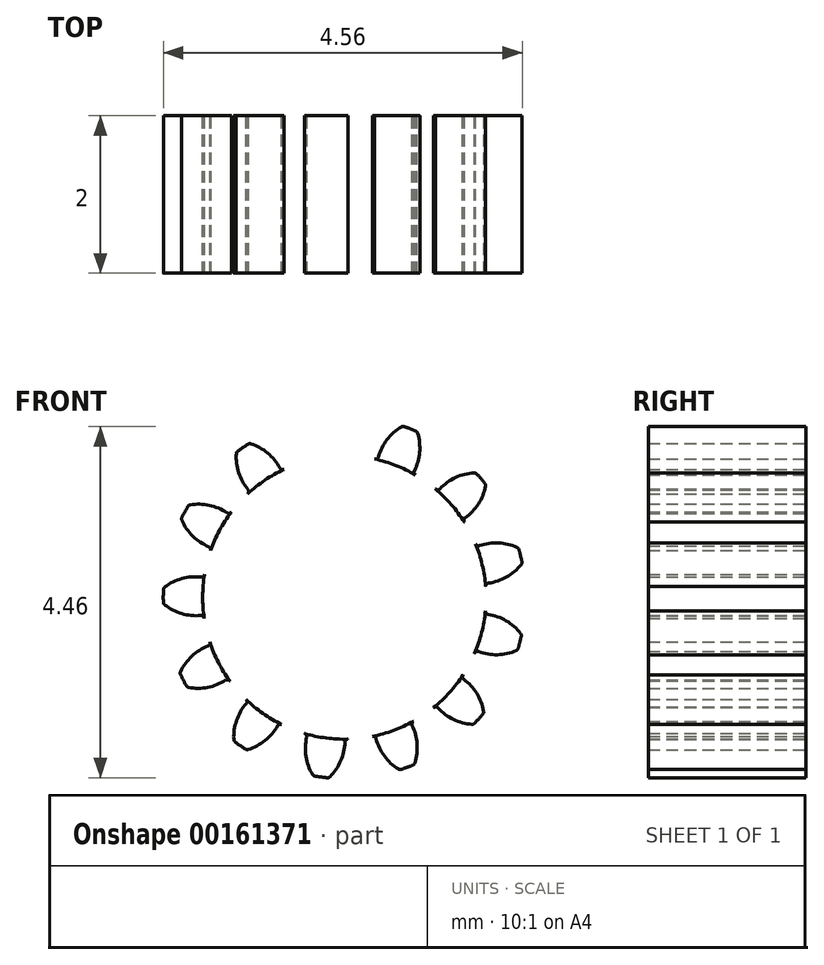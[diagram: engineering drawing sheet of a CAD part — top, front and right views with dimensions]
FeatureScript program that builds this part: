
annotation { "Feature Type Name" : "Feature", "Feature Type Description" : "" }
export const myFeature = defineFeature(function(context is Context, id is Id, definition is map)
    precondition{}
    {
        {
            var Q0;
            Q0=qCreatedBy(makeId("Front.planeOp"),FACE);
            var sketch = newSketch(context, id + "F0", { "sketchPlane" : qUnion([Q0])});
            skCircle(sketch, "E0", {"center": v(0, 0) * mm, "radius": 1.8 * mm, "construction": true});
            skCircle(sketch, "E1", {"center": v(0, 0) * mm, "radius": 2.05 * mm, "construction": true});
            skCircle(sketch, "E2", {"center": v(0, 0) * mm, "radius": 2.3 * mm, "construction": true});
            skLineSegment(sketch, "E3", {"start": v(0, 8.23) * mm, "end": v(0, 0) * mm, "construction": true});
            skCircle(sketch, "E4.cCircle", {"center": v(0, 0) * mm, "radius": 8.23 * mm, "construction": true});
            skLineSegment(sketch, "E4.0", {"start": v(0, 8.23) * mm, "end": v(1.83, 8.03) * mm, "construction": true});
            skLineSegment(sketch, "E4.1", {"start": v(1.83, 8.03) * mm, "end": v(3.57, 7.42) * mm, "construction": true});
            skLineSegment(sketch, "E4.2", {"start": v(3.57, 7.42) * mm, "end": v(5.13, 6.44) * mm, "construction": true});
            skLineSegment(sketch, "E4.3", {"start": v(5.13, 6.44) * mm, "end": v(6.44, 5.13) * mm, "construction": true});
            skLineSegment(sketch, "E4.4", {"start": v(6.44, 5.13) * mm, "end": v(7.42, 3.57) * mm, "construction": true});
            skLineSegment(sketch, "E4.5", {"start": v(7.42, 3.57) * mm, "end": v(8.03, 1.83) * mm, "construction": true});
            skLineSegment(sketch, "E4.6", {"start": v(8.03, 1.83) * mm, "end": v(8.23, 0) * mm, "construction": true});
            skLineSegment(sketch, "E4.7", {"start": v(8.23, 0) * mm, "end": v(8.03, -1.83) * mm, "construction": true});
            skLineSegment(sketch, "E4.8", {"start": v(8.03, -1.83) * mm, "end": v(7.42, -3.57) * mm, "construction": true});
            skLineSegment(sketch, "E4.9", {"start": v(7.42, -3.57) * mm, "end": v(6.44, -5.13) * mm, "construction": true});
            skLineSegment(sketch, "E4.10", {"start": v(6.44, -5.13) * mm, "end": v(5.13, -6.44) * mm, "construction": true});
            skLineSegment(sketch, "E4.11", {"start": v(5.13, -6.44) * mm, "end": v(3.57, -7.42) * mm, "construction": true});
            skLineSegment(sketch, "E4.12", {"start": v(3.57, -7.42) * mm, "end": v(1.83, -8.03) * mm, "construction": true});
            skLineSegment(sketch, "E4.13", {"start": v(1.83, -8.03) * mm, "end": v(0, -8.23) * mm, "construction": true});
            skLineSegment(sketch, "E4.14", {"start": v(0, -8.23) * mm, "end": v(-1.83, -8.03) * mm, "construction": true});
            skLineSegment(sketch, "E4.15", {"start": v(-1.83, -8.03) * mm, "end": v(-3.57, -7.42) * mm, "construction": true});
            skLineSegment(sketch, "E4.16", {"start": v(-3.57, -7.42) * mm, "end": v(-5.13, -6.44) * mm, "construction": true});
            skLineSegment(sketch, "E4.17", {"start": v(-5.13, -6.44) * mm, "end": v(-6.44, -5.13) * mm, "construction": true});
            skLineSegment(sketch, "E4.18", {"start": v(-6.44, -5.13) * mm, "end": v(-7.42, -3.57) * mm, "construction": true});
            skLineSegment(sketch, "E4.19", {"start": v(-7.42, -3.57) * mm, "end": v(-8.03, -1.83) * mm, "construction": true});
            skLineSegment(sketch, "E4.20", {"start": v(-8.03, -1.83) * mm, "end": v(-8.23, 0) * mm, "construction": true});
            skLineSegment(sketch, "E4.21", {"start": v(-8.23, 0) * mm, "end": v(-8.03, 1.83) * mm, "construction": true});
            skLineSegment(sketch, "E4.22", {"start": v(-8.03, 1.83) * mm, "end": v(-7.42, 3.57) * mm, "construction": true});
            skLineSegment(sketch, "E4.23", {"start": v(-7.42, 3.57) * mm, "end": v(-6.44, 5.13) * mm, "construction": true});
            skLineSegment(sketch, "E4.24", {"start": v(-6.44, 5.13) * mm, "end": v(-5.13, 6.44) * mm, "construction": true});
            skLineSegment(sketch, "E4.25", {"start": v(-5.13, 6.44) * mm, "end": v(-3.57, 7.42) * mm, "construction": true});
            skLineSegment(sketch, "E4.26", {"start": v(-3.57, 7.42) * mm, "end": v(-1.83, 8.03) * mm, "construction": true});
            skLineSegment(sketch, "E4.27", {"start": v(-1.83, 8.03) * mm, "end": v(0, 8.23) * mm, "construction": true});
            skLineSegment(sketch, "E5.0", {"start": v(-0.93, 8.23) * mm, "end": v(0.93, 8.23) * mm, "construction": true});
            skLineSegment(sketch, "E5.1", {"start": v(0.93, 8.23) * mm, "end": v(2.74, 7.82) * mm, "construction": true});
            skLineSegment(sketch, "E5.2", {"start": v(2.74, 7.82) * mm, "end": v(4.4, 7.02) * mm, "construction": true});
            skLineSegment(sketch, "E5.3", {"start": v(4.4, 7.02) * mm, "end": v(5.86, 5.86) * mm});
            skLineSegment(sketch, "E5.4", {"start": v(5.86, 5.86) * mm, "end": v(7.02, 4.4) * mm});
            skLineSegment(sketch, "E5.5", {"start": v(7.02, 4.4) * mm, "end": v(7.82, 2.74) * mm});
            skLineSegment(sketch, "E5.6", {"start": v(7.82, 2.74) * mm, "end": v(8.23, 0.93) * mm});
            skLineSegment(sketch, "E5.7", {"start": v(8.23, 0.93) * mm, "end": v(8.23, -0.93) * mm});
            skLineSegment(sketch, "E5.8", {"start": v(8.23, -0.93) * mm, "end": v(7.82, -2.74) * mm});
            skLineSegment(sketch, "E5.9", {"start": v(7.82, -2.74) * mm, "end": v(7.02, -4.4) * mm});
            skLineSegment(sketch, "E5.10", {"start": v(7.02, -4.4) * mm, "end": v(5.86, -5.86) * mm});
            skLineSegment(sketch, "E5.11", {"start": v(5.86, -5.86) * mm, "end": v(4.4, -7.02) * mm});
            skLineSegment(sketch, "E5.12", {"start": v(4.4, -7.02) * mm, "end": v(2.74, -7.82) * mm});
            skLineSegment(sketch, "E5.13", {"start": v(2.74, -7.82) * mm, "end": v(0.93, -8.23) * mm});
            skLineSegment(sketch, "E5.14", {"start": v(0.93, -8.23) * mm, "end": v(-0.93, -8.23) * mm});
            skLineSegment(sketch, "E5.15", {"start": v(-0.93, -8.23) * mm, "end": v(-2.74, -7.82) * mm});
            skLineSegment(sketch, "E5.16", {"start": v(-2.74, -7.82) * mm, "end": v(-4.4, -7.02) * mm});
            skLineSegment(sketch, "E5.17", {"start": v(-4.4, -7.02) * mm, "end": v(-5.86, -5.86) * mm});
            skLineSegment(sketch, "E5.18", {"start": v(-5.86, -5.86) * mm, "end": v(-7.02, -4.4) * mm});
            skLineSegment(sketch, "E5.19", {"start": v(-7.02, -4.4) * mm, "end": v(-7.82, -2.74) * mm});
            skLineSegment(sketch, "E5.20", {"start": v(-7.82, -2.74) * mm, "end": v(-8.23, -0.93) * mm});
            skLineSegment(sketch, "E5.21", {"start": v(-8.23, -0.93) * mm, "end": v(-8.23, 0.93) * mm});
            skLineSegment(sketch, "E5.22", {"start": v(-8.23, 0.93) * mm, "end": v(-7.82, 2.74) * mm});
            skLineSegment(sketch, "E5.23", {"start": v(-7.82, 2.74) * mm, "end": v(-7.02, 4.4) * mm});
            skLineSegment(sketch, "E5.24", {"start": v(-7.02, 4.4) * mm, "end": v(-5.86, 5.86) * mm});
            skLineSegment(sketch, "E5.25", {"start": v(-5.86, 5.86) * mm, "end": v(-4.4, 7.02) * mm, "construction": true});
            skLineSegment(sketch, "E5.26", {"start": v(-4.4, 7.02) * mm, "end": v(-2.74, 7.82) * mm, "construction": true});
            skLineSegment(sketch, "E5.27", {"start": v(-2.74, 7.82) * mm, "end": v(-0.93, 8.23) * mm, "construction": true});
            skPoint(sketch, "E5.0.midPoint", {"position": v(0, 8.23) * mm});
            skLineSegment(sketch, "E6", {"start": v(-0.93, 8.23) * mm, "end": v(0, 0) * mm, "construction": true});
            skLineSegment(sketch, "E7", {"start": v(0, 2.05) * mm, "end": v(-9.32, 2.05) * mm, "construction": true});
            skLineSegment(sketch, "E8", {"start": v(0, 2.05) * mm, "end": v(-5.63, 0) * mm, "construction": true});
            skCircle(sketch, "E9", {"center": v(0, 2.05) * mm, "radius": 0.65 * mm, "construction": true});
            skCircle(sketch, "E10", {"center": v(-0.61, 1.83) * mm, "radius": 0.65 * mm, "construction": true});
            skArc(sketch, "E11", {"start": v(-0.15, 2.28) * mm, "mid": v(-0.01, 2.08) * mm, "end": v(0.04, 1.84) * mm});
            skArc(sketch, "E12.MirrorCS", {"start": v(-0.36, 2.27) * mm, "mid": v(-0.45, 2.02) * mm, "end": v(-0.44, 1.75) * mm});
            skArc(sketch, "E13.MirrorCS", {"start": v(-0.37, 2.26) * mm, "mid": v(-0.45, 2.03) * mm, "end": v(-0.45, 1.78) * mm});
            skArc(sketch, "E14", {"start": v(-0.34, 2.28) * mm, "mid": v(-0.26, 2.29) * mm, "end": v(-0.18, 2.3) * mm});
            skArc(sketch, "E15", {"start": v(-0.48, 1.74) * mm, "mid": v(0.2, -1.79) * mm, "end": v(0.08, 1.8) * mm});
            skPoint(sketch, "E16.visualSharp", {"position": v(-0.44, 1.75) * mm});
            skArc(sketch, "E16.filletArc", {"start": v(-0.48, 1.74) * mm, "mid": v(-0.45, 1.75) * mm, "end": v(-0.45, 1.78) * mm});
            skPoint(sketch, "E17.visualSharp", {"position": v(0.04, 1.8) * mm});
            skArc(sketch, "E17.filletArc", {"start": v(0.04, 1.84) * mm, "mid": v(0.05, 1.81) * mm, "end": v(0.08, 1.8) * mm});
            skPoint(sketch, "E18.visualSharp", {"position": v(-0.36, 2.27) * mm});
            skArc(sketch, "E18.filletArc", {"start": v(-0.34, 2.28) * mm, "mid": v(-0.35, 2.27) * mm, "end": v(-0.37, 2.26) * mm});
            skPoint(sketch, "E19.visualSharp", {"position": v(-0.16, 2.3) * mm});
            skArc(sketch, "E19.filletArc", {"start": v(-0.15, 2.28) * mm, "mid": v(-0.16, 2.3) * mm, "end": v(-0.18, 2.3) * mm});
            skArc(sketch, "E20.1.0", {"start": v(-1.37, 1.83) * mm, "mid": v(-1.34, 1.59) * mm, "end": v(-1.22, 1.37) * mm});
            skArc(sketch, "E20.1.1", {"start": v(-1.23, 1.32) * mm, "mid": v(-1.22, 1.34) * mm, "end": v(-1.22, 1.37) * mm});
            skArc(sketch, "E20.1.2", {"start": v(-1.36, 1.86) * mm, "mid": v(-1.37, 1.84) * mm, "end": v(-1.37, 1.83) * mm});
            skArc(sketch, "E20.1.3", {"start": v(-1.36, 1.86) * mm, "mid": v(-1.3, 1.9) * mm, "end": v(-1.22, 1.95) * mm});
            skArc(sketch, "E20.1.4", {"start": v(-1.19, 1.95) * mm, "mid": v(-0.97, 1.83) * mm, "end": v(-0.82, 1.65) * mm});
            skArc(sketch, "E20.1.5", {"start": v(-1.19, 1.95) * mm, "mid": v(-1.2, 1.95) * mm, "end": v(-1.22, 1.95) * mm});
            skArc(sketch, "E20.1.6", {"start": v(-0.82, 1.65) * mm, "mid": v(-0.8, 1.63) * mm, "end": v(-0.77, 1.63) * mm});
            skArc(sketch, "E20.2.0", {"start": v(-2.06, 0.98) * mm, "mid": v(-1.93, 0.78) * mm, "end": v(-1.72, 0.64) * mm});
            skArc(sketch, "E20.2.1", {"start": v(-1.7, 0.6) * mm, "mid": v(-1.7, 0.62) * mm, "end": v(-1.72, 0.64) * mm});
            skArc(sketch, "E20.2.2", {"start": v(-2.06, 1.01) * mm, "mid": v(-2.07, 1) * mm, "end": v(-2.06, 0.98) * mm});
            skArc(sketch, "E20.2.3", {"start": v(-2.06, 1.01) * mm, "mid": v(-2.03, 1.09) * mm, "end": v(-1.99, 1.16) * mm});
            skArc(sketch, "E20.2.4", {"start": v(-1.96, 1.18) * mm, "mid": v(-1.72, 1.17) * mm, "end": v(-1.5, 1.08) * mm});
            skArc(sketch, "E20.2.5", {"start": v(-1.96, 1.18) * mm, "mid": v(-1.98, 1.17) * mm, "end": v(-1.99, 1.16) * mm});
            skArc(sketch, "E20.2.6", {"start": v(-1.5, 1.08) * mm, "mid": v(-1.46, 1.07) * mm, "end": v(-1.44, 1.09) * mm});
            skArc(sketch, "E20.3.0", {"start": v(-2.28, -0.1) * mm, "mid": v(-2.07, -0.2) * mm, "end": v(-1.82, -0.23) * mm});
            skArc(sketch, "E20.3.1", {"start": v(-1.78, -0.26) * mm, "mid": v(-1.8, -0.24) * mm, "end": v(-1.82, -0.23) * mm});
            skArc(sketch, "E20.3.2", {"start": v(-2.3, -0.06) * mm, "mid": v(-2.3, -0.08) * mm, "end": v(-2.28, -0.1) * mm});
            skArc(sketch, "E20.3.3", {"start": v(-2.3, -0.06) * mm, "mid": v(-2.3, 0.02) * mm, "end": v(-2.3, 0.1) * mm});
            skArc(sketch, "E20.3.4", {"start": v(-2.28, 0.13) * mm, "mid": v(-2.06, 0.24) * mm, "end": v(-1.82, 0.26) * mm});
            skArc(sketch, "E20.3.5", {"start": v(-2.28, 0.13) * mm, "mid": v(-2.3, 0.12) * mm, "end": v(-2.3, 0.1) * mm});
            skArc(sketch, "E20.3.6", {"start": v(-1.82, 0.26) * mm, "mid": v(-1.8, 0.27) * mm, "end": v(-1.78, 0.3) * mm});
            skArc(sketch, "E20.4.0", {"start": v(-1.98, -1.14) * mm, "mid": v(-1.74, -1.14) * mm, "end": v(-1.5, -1.05) * mm});
            skArc(sketch, "E20.4.1", {"start": v(-1.45, -1.06) * mm, "mid": v(-1.48, -1.04) * mm, "end": v(-1.5, -1.05) * mm});
            skArc(sketch, "E20.4.2", {"start": v(-2, -1.12) * mm, "mid": v(-2, -1.14) * mm, "end": v(-1.98, -1.14) * mm});
            skArc(sketch, "E20.4.3", {"start": v(-2, -1.12) * mm, "mid": v(-2.05, -1.05) * mm, "end": v(-2.08, -0.98) * mm});
            skArc(sketch, "E20.4.4", {"start": v(-2.08, -0.94) * mm, "mid": v(-1.94, -0.75) * mm, "end": v(-1.73, -0.62) * mm});
            skArc(sketch, "E20.4.5", {"start": v(-2.08, -0.94) * mm, "mid": v(-2.09, -0.96) * mm, "end": v(-2.08, -0.98) * mm});
            skArc(sketch, "E20.4.6", {"start": v(-1.73, -0.62) * mm, "mid": v(-1.71, -0.6) * mm, "end": v(-1.7, -0.57) * mm});
            skArc(sketch, "E20.5.0", {"start": v(-1.22, -1.93) * mm, "mid": v(-1, -1.82) * mm, "end": v(-0.85, -1.63) * mm});
            skArc(sketch, "E20.5.1", {"start": v(-0.8, -1.61) * mm, "mid": v(-0.82, -1.61) * mm, "end": v(-0.85, -1.63) * mm});
            skArc(sketch, "E20.5.2", {"start": v(-1.26, -1.93) * mm, "mid": v(-1.24, -1.93) * mm, "end": v(-1.22, -1.93) * mm});
            skArc(sketch, "E20.5.3", {"start": v(-1.26, -1.93) * mm, "mid": v(-1.32, -1.88) * mm, "end": v(-1.39, -1.83) * mm});
            skArc(sketch, "E20.5.4", {"start": v(-1.4, -1.8) * mm, "mid": v(-1.37, -1.56) * mm, "end": v(-1.25, -1.35) * mm});
            skArc(sketch, "E20.5.5", {"start": v(-1.4, -1.8) * mm, "mid": v(-1.4, -1.82) * mm, "end": v(-1.39, -1.83) * mm});
            skArc(sketch, "E20.5.6", {"start": v(-1.25, -1.35) * mm, "mid": v(-1.24, -1.32) * mm, "end": v(-1.25, -1.3) * mm});
            skArc(sketch, "E20.6.0", {"start": v(-0.18, -2.28) * mm, "mid": v(-0.05, -2.08) * mm, "end": v(0, -1.84) * mm});
            skArc(sketch, "E20.6.1", {"start": v(0.05, -1.8) * mm, "mid": v(0.02, -1.81) * mm, "end": v(0, -1.84) * mm});
            skArc(sketch, "E20.6.2", {"start": v(-0.22, -2.29) * mm, "mid": v(-0.2, -2.29) * mm, "end": v(-0.18, -2.28) * mm});
            skArc(sketch, "E20.6.3", {"start": v(-0.22, -2.29) * mm, "mid": v(-0.3, -2.28) * mm, "end": v(-0.38, -2.27) * mm});
            skArc(sketch, "E20.6.4", {"start": v(-0.4, -2.25) * mm, "mid": v(-0.49, -2.02) * mm, "end": v(-0.48, -1.77) * mm});
            skArc(sketch, "E20.6.5", {"start": v(-0.4, -2.25) * mm, "mid": v(-0.4, -2.26) * mm, "end": v(-0.38, -2.27) * mm});
            skArc(sketch, "E20.6.6", {"start": v(-0.48, -1.77) * mm, "mid": v(-0.48, -1.75) * mm, "end": v(-0.5, -1.73) * mm});
            skArc(sketch, "E20.7.0", {"start": v(0.9, -2.1) * mm, "mid": v(0.92, -1.86) * mm, "end": v(0.86, -1.62) * mm});
            skArc(sketch, "E20.7.1", {"start": v(0.88, -1.57) * mm, "mid": v(0.86, -1.6) * mm, "end": v(0.86, -1.62) * mm});
            skArc(sketch, "E20.7.2", {"start": v(0.87, -2.13) * mm, "mid": v(0.89, -2.12) * mm, "end": v(0.9, -2.1) * mm});
            skArc(sketch, "E20.7.3", {"start": v(0.87, -2.13) * mm, "mid": v(0.8, -2.16) * mm, "end": v(0.72, -2.18) * mm});
            skArc(sketch, "E20.7.4", {"start": v(0.69, -2.18) * mm, "mid": v(0.5, -2.01) * mm, "end": v(0.4, -1.8) * mm});
            skArc(sketch, "E20.7.5", {"start": v(0.69, -2.18) * mm, "mid": v(0.7, -2.19) * mm, "end": v(0.72, -2.18) * mm});
            skArc(sketch, "E20.7.6", {"start": v(0.4, -1.8) * mm, "mid": v(0.38, -1.77) * mm, "end": v(0.36, -1.76) * mm});
            skArc(sketch, "E20.8.0", {"start": v(1.77, -1.45) * mm, "mid": v(1.68, -1.22) * mm, "end": v(1.52, -1.04) * mm});
            skArc(sketch, "E20.8.1", {"start": v(1.5, -0.98) * mm, "mid": v(1.5, -1.01) * mm, "end": v(1.52, -1.04) * mm});
            skArc(sketch, "E20.8.2", {"start": v(1.76, -1.48) * mm, "mid": v(1.77, -1.46) * mm, "end": v(1.77, -1.45) * mm});
            skArc(sketch, "E20.8.3", {"start": v(1.76, -1.48) * mm, "mid": v(1.7, -1.54) * mm, "end": v(1.65, -1.6) * mm});
            skArc(sketch, "E20.8.4", {"start": v(1.62, -1.61) * mm, "mid": v(1.39, -1.55) * mm, "end": v(1.19, -1.4) * mm});
            skArc(sketch, "E20.8.5", {"start": v(1.62, -1.61) * mm, "mid": v(1.64, -1.6) * mm, "end": v(1.65, -1.6) * mm});
            skArc(sketch, "E20.8.6", {"start": v(1.19, -1.4) * mm, "mid": v(1.16, -1.39) * mm, "end": v(1.13, -1.4) * mm});
            skArc(sketch, "E20.9.0", {"start": v(2.24, -0.46) * mm, "mid": v(2.06, -0.3) * mm, "end": v(1.83, -0.21) * mm});
            skArc(sketch, "E20.9.1", {"start": v(1.8, -0.17) * mm, "mid": v(1.8, -0.2) * mm, "end": v(1.83, -0.21) * mm});
            skArc(sketch, "E20.9.2", {"start": v(2.25, -0.5) * mm, "mid": v(2.25, -0.47) * mm, "end": v(2.24, -0.46) * mm});
            skArc(sketch, "E20.9.3", {"start": v(2.25, -0.5) * mm, "mid": v(2.23, -0.57) * mm, "end": v(2.2, -0.65) * mm});
            skArc(sketch, "E20.9.4", {"start": v(2.18, -0.67) * mm, "mid": v(1.95, -0.73) * mm, "end": v(1.7, -0.69) * mm});
            skArc(sketch, "E20.9.5", {"start": v(2.18, -0.67) * mm, "mid": v(2.2, -0.66) * mm, "end": v(2.2, -0.65) * mm});
            skArc(sketch, "E20.9.6", {"start": v(1.7, -0.69) * mm, "mid": v(1.67, -0.69) * mm, "end": v(1.65, -0.71) * mm});
            skArc(sketch, "E20.10.0", {"start": v(2.2, 0.64) * mm, "mid": v(1.96, 0.7) * mm, "end": v(1.72, 0.66) * mm});
            skArc(sketch, "E20.10.1", {"start": v(1.67, 0.68) * mm, "mid": v(1.69, 0.66) * mm, "end": v(1.72, 0.66) * mm});
            skArc(sketch, "E20.10.2", {"start": v(2.22, 0.6) * mm, "mid": v(2.2, 0.62) * mm, "end": v(2.2, 0.64) * mm});
            skArc(sketch, "E20.10.3", {"start": v(2.22, 0.6) * mm, "mid": v(2.24, 0.53) * mm, "end": v(2.26, 0.45) * mm});
            skArc(sketch, "E20.10.4", {"start": v(2.25, 0.42) * mm, "mid": v(2.06, 0.26) * mm, "end": v(1.83, 0.18) * mm});
            skArc(sketch, "E20.10.5", {"start": v(2.25, 0.42) * mm, "mid": v(2.25, 0.43) * mm, "end": v(2.26, 0.45) * mm});
            skArc(sketch, "E20.10.6", {"start": v(1.83, 0.18) * mm, "mid": v(1.8, 0.17) * mm, "end": v(1.8, 0.14) * mm});
            skArc(sketch, "E20.11.0", {"start": v(1.65, 1.58) * mm, "mid": v(1.41, 1.52) * mm, "end": v(1.21, 1.38) * mm});
            skArc(sketch, "E20.11.1", {"start": v(1.16, 1.38) * mm, "mid": v(1.19, 1.37) * mm, "end": v(1.21, 1.38) * mm});
            skArc(sketch, "E20.11.2", {"start": v(1.68, 1.57) * mm, "mid": v(1.67, 1.58) * mm, "end": v(1.65, 1.58) * mm});
            skArc(sketch, "E20.11.3", {"start": v(1.68, 1.57) * mm, "mid": v(1.73, 1.51) * mm, "end": v(1.79, 1.45) * mm});
            skArc(sketch, "E20.11.4", {"start": v(1.8, 1.42) * mm, "mid": v(1.7, 1.19) * mm, "end": v(1.53, 1.01) * mm});
            skArc(sketch, "E20.11.5", {"start": v(1.8, 1.42) * mm, "mid": v(1.8, 1.43) * mm, "end": v(1.79, 1.45) * mm});
            skArc(sketch, "E20.11.6", {"start": v(1.53, 1.01) * mm, "mid": v(1.52, 0.99) * mm, "end": v(1.52, 0.96) * mm});
            skArc(sketch, "E20.12.0", {"start": v(0.72, 2.17) * mm, "mid": v(0.54, 2) * mm, "end": v(0.43, 1.79) * mm});
            skArc(sketch, "E20.12.1", {"start": v(0.39, 1.76) * mm, "mid": v(0.41, 1.76) * mm, "end": v(0.43, 1.79) * mm});
            skArc(sketch, "E20.12.2", {"start": v(0.76, 2.17) * mm, "mid": v(0.74, 2.17) * mm, "end": v(0.72, 2.17) * mm});
            skArc(sketch, "E20.12.3", {"start": v(0.76, 2.17) * mm, "mid": v(0.83, 2.14) * mm, "end": v(0.9, 2.11) * mm});
            skArc(sketch, "E20.12.4", {"start": v(0.93, 2.09) * mm, "mid": v(0.96, 1.84) * mm, "end": v(0.89, 1.6) * mm});
            skArc(sketch, "E20.12.5", {"start": v(0.93, 2.09) * mm, "mid": v(0.92, 2.1) * mm, "end": v(0.9, 2.11) * mm});
            skArc(sketch, "E20.12.6", {"start": v(0.89, 1.6) * mm, "mid": v(0.89, 1.58) * mm, "end": v(0.9, 1.56) * mm});
            skSolve(sketch);
        }
        {
            var Q0;
            Q0=makeQuery(id+"F0.imprint","IMPRINT",FACE,{"disambiguationData":[TD([[makeQuery(id+"F0.imprint","IMPRINT",EDGE,{"derivedFrom":sQuery(id+"F0.wireOp",EDGE,"E11")}),-1.0]])]});
            var Q1;
            Q1=makeQuery(id+"F0.imprint","IMPRINT",FACE,{"disambiguationData":[TD([[makeQuery(id+"F0.imprint","IMPRINT",EDGE,{"derivedFrom":sQuery(id+"F0.wireOp",EDGE,"E20.1.0")}),1.0]])]});
            var Q2;
            Q2=makeQuery(id+"F0.imprint","IMPRINT",FACE,{"disambiguationData":[TD([[makeQuery(id+"F0.imprint","IMPRINT",EDGE,{"derivedFrom":sQuery(id+"F0.wireOp",EDGE,"E20.3.0")}),1.0]])]});
            var Q3;
            Q3=makeQuery(id+"F0.imprint","IMPRINT",FACE,{"disambiguationData":[TD([[makeQuery(id+"F0.imprint","IMPRINT",EDGE,{"derivedFrom":sQuery(id+"F0.wireOp",EDGE,"E20.5.0")}),1.0]])]});
            var Q4;
            Q4=makeQuery(id+"F0.imprint","IMPRINT",FACE,{"disambiguationData":[TD([[makeQuery(id+"F0.imprint","IMPRINT",EDGE,{"derivedFrom":sQuery(id+"F0.wireOp",EDGE,"E20.6.0")}),1.0]])]});
            var Q5;
            Q5=makeQuery(id+"F0.imprint","IMPRINT",FACE,{"disambiguationData":[TD([[makeQuery(id+"F0.imprint","IMPRINT",EDGE,{"derivedFrom":sQuery(id+"F0.wireOp",EDGE,"E20.7.0")}),1.0]])]});
            var Q6;
            Q6=makeQuery(id+"F0.imprint","IMPRINT",FACE,{"disambiguationData":[TD([[makeQuery(id+"F0.imprint","IMPRINT",EDGE,{"derivedFrom":sQuery(id+"F0.wireOp",EDGE,"E20.8.0")}),1.0]])]});
            var Q7;
            Q7=makeQuery(id+"F0.imprint","IMPRINT",FACE,{"disambiguationData":[TD([[makeQuery(id+"F0.imprint","IMPRINT",EDGE,{"derivedFrom":sQuery(id+"F0.wireOp",EDGE,"E20.9.0")}),1.0]])]});
            var Q8;
            Q8=makeQuery(id+"F0.imprint","IMPRINT",FACE,{"disambiguationData":[TD([[makeQuery(id+"F0.imprint","IMPRINT",EDGE,{"derivedFrom":sQuery(id+"F0.wireOp",EDGE,"E20.10.0")}),1.0]])]});
            var Q9;
            Q9=makeQuery(id+"F0.imprint","IMPRINT",FACE,{"disambiguationData":[TD([[makeQuery(id+"F0.imprint","IMPRINT",EDGE,{"derivedFrom":sQuery(id+"F0.wireOp",EDGE,"E20.11.0")}),1.0]])]});
            var Q10;
            Q10=makeQuery(id+"F0.imprint","IMPRINT",FACE,{"disambiguationData":[TD([[makeQuery(id+"F0.imprint","IMPRINT",EDGE,{"derivedFrom":sQuery(id+"F0.wireOp",EDGE,"E20.12.0")}),1.0]])]});
            var Q11;
            Q11=makeQuery(id+"F0.imprint","IMPRINT",FACE,{"disambiguationData":[TD([[makeQuery(id+"F0.imprint","IMPRINT",EDGE,{"derivedFrom":sQuery(id+"F0.wireOp",EDGE,"E20.13.0")}),1.0]])]});
            var Q12;
            Q12=makeQuery(id+"F0.imprint","IMPRINT",FACE,{"disambiguationData":[TD([[makeQuery(id+"F0.imprint","IMPRINT",EDGE,{"derivedFrom":sQuery(id+"F0.wireOp",EDGE,"E20.2.0")}),1.0]])]});
            var Q13;
            Q13=makeQuery(id+"F0.imprint","IMPRINT",FACE,{"disambiguationData":[TD([[makeQuery(id+"F0.imprint","IMPRINT",EDGE,{"derivedFrom":sQuery(id+"F0.wireOp",EDGE,"E20.4.0")}),1.0]])]});
            extrude(context, id + "F1", {"entities" : qUnion([Q0, Q1, Q2, Q3, Q4, Q5, Q6, Q7, Q8, Q9, Q10, Q11, Q12, Q13]), "depth" : 2 * mm});
        }
        {
            var Q0;
            Q0=makeQuery(id+"F1.opExtrude","CAP_FACE",FACE,{"disambiguationData":[OSD([sQuery(id+"F0.wireOp",EDGE,"E11"),sQuery(id+"F0.wireOp",EDGE,"E13.MirrorCS"),sQuery(id+"F0.wireOp",EDGE,"E14"),sQuery(id+"F0.wireOp",EDGE,"E15"),sQuery(id+"F0.wireOp",EDGE,"E16.filletArc"),sQuery(id+"F0.wireOp",EDGE,"E17.filletArc"),sQuery(id+"F0.wireOp",EDGE,"E18.filletArc"),sQuery(id+"F0.wireOp",EDGE,"E19.filletArc"),sQuery(id+"F0.wireOp",EDGE,"E20.1.0"),sQuery(id+"F0.wireOp",EDGE,"E20.1.1"),sQuery(id+"F0.wireOp",EDGE,"E20.1.2"),sQuery(id+"F0.wireOp",EDGE,"E20.1.3"),sQuery(id+"F0.wireOp",EDGE,"E20.1.4"),sQuery(id+"F0.wireOp",EDGE,"E20.1.5"),sQuery(id+"F0.wireOp",EDGE,"E20.1.6"),sQuery(id+"F0.wireOp",EDGE,"E20.2.0"),sQuery(id+"F0.wireOp",EDGE,"E20.2.1"),sQuery(id+"F0.wireOp",EDGE,"E20.2.2"),sQuery(id+"F0.wireOp",EDGE,"E20.2.3"),sQuery(id+"F0.wireOp",EDGE,"E20.2.4"),sQuery(id+"F0.wireOp",EDGE,"E20.2.5"),sQuery(id+"F0.wireOp",EDGE,"E20.2.6"),sQuery(id+"F0.wireOp",EDGE,"E20.3.0"),sQuery(id+"F0.wireOp",EDGE,"E20.3.1"),sQuery(id+"F0.wireOp",EDGE,"E20.3.2"),sQuery(id+"F0.wireOp",EDGE,"E20.3.3"),sQuery(id+"F0.wireOp",EDGE,"E20.3.4"),sQuery(id+"F0.wireOp",EDGE,"E20.3.5"),sQuery(id+"F0.wireOp",EDGE,"E20.3.6"),sQuery(id+"F0.wireOp",EDGE,"E20.4.0"),sQuery(id+"F0.wireOp",EDGE,"E20.4.1"),sQuery(id+"F0.wireOp",EDGE,"E20.4.2"),sQuery(id+"F0.wireOp",EDGE,"E20.4.3"),sQuery(id+"F0.wireOp",EDGE,"E20.4.4"),sQuery(id+"F0.wireOp",EDGE,"E20.4.5"),sQuery(id+"F0.wireOp",EDGE,"E20.4.6"),sQuery(id+"F0.wireOp",EDGE,"E20.5.0"),sQuery(id+"F0.wireOp",EDGE,"E20.5.1"),sQuery(id+"F0.wireOp",EDGE,"E20.5.2"),sQuery(id+"F0.wireOp",EDGE,"E20.5.3"),sQuery(id+"F0.wireOp",EDGE,"E20.5.4"),sQuery(id+"F0.wireOp",EDGE,"E20.5.5"),sQuery(id+"F0.wireOp",EDGE,"E20.5.6"),sQuery(id+"F0.wireOp",EDGE,"E20.6.0"),sQuery(id+"F0.wireOp",EDGE,"E20.6.1"),sQuery(id+"F0.wireOp",EDGE,"E20.6.2"),sQuery(id+"F0.wireOp",EDGE,"E20.6.3"),sQuery(id+"F0.wireOp",EDGE,"E20.6.4"),sQuery(id+"F0.wireOp",EDGE,"E20.6.5"),sQuery(id+"F0.wireOp",EDGE,"E20.6.6"),sQuery(id+"F0.wireOp",EDGE,"E20.7.0"),sQuery(id+"F0.wireOp",EDGE,"E20.7.1"),sQuery(id+"F0.wireOp",EDGE,"E20.7.2"),sQuery(id+"F0.wireOp",EDGE,"E20.7.3"),sQuery(id+"F0.wireOp",EDGE,"E20.7.4"),sQuery(id+"F0.wireOp",EDGE,"E20.7.5"),sQuery(id+"F0.wireOp",EDGE,"E20.7.6"),sQuery(id+"F0.wireOp",EDGE,"E20.8.0"),sQuery(id+"F0.wireOp",EDGE,"E20.8.1"),sQuery(id+"F0.wireOp",EDGE,"E20.8.2"),sQuery(id+"F0.wireOp",EDGE,"E20.8.3"),sQuery(id+"F0.wireOp",EDGE,"E20.8.4"),sQuery(id+"F0.wireOp",EDGE,"E20.8.5"),sQuery(id+"F0.wireOp",EDGE,"E20.8.6"),sQuery(id+"F0.wireOp",EDGE,"E20.9.0"),sQuery(id+"F0.wireOp",EDGE,"E20.9.1"),sQuery(id+"F0.wireOp",EDGE,"E20.9.2"),sQuery(id+"F0.wireOp",EDGE,"E20.9.3"),sQuery(id+"F0.wireOp",EDGE,"E20.9.4"),sQuery(id+"F0.wireOp",EDGE,"E20.9.5"),sQuery(id+"F0.wireOp",EDGE,"E20.9.6"),sQuery(id+"F0.wireOp",EDGE,"E20.10.0"),sQuery(id+"F0.wireOp",EDGE,"E20.10.1"),sQuery(id+"F0.wireOp",EDGE,"E20.10.2"),sQuery(id+"F0.wireOp",EDGE,"E20.10.3"),sQuery(id+"F0.wireOp",EDGE,"E20.10.4"),sQuery(id+"F0.wireOp",EDGE,"E20.10.5"),sQuery(id+"F0.wireOp",EDGE,"E20.10.6"),sQuery(id+"F0.wireOp",EDGE,"E20.11.0"),sQuery(id+"F0.wireOp",EDGE,"E20.11.1"),sQuery(id+"F0.wireOp",EDGE,"E20.11.2"),sQuery(id+"F0.wireOp",EDGE,"E20.11.3"),sQuery(id+"F0.wireOp",EDGE,"E20.11.4"),sQuery(id+"F0.wireOp",EDGE,"E20.11.5"),sQuery(id+"F0.wireOp",EDGE,"E20.11.6"),sQuery(id+"F0.wireOp",EDGE,"E20.12.0"),sQuery(id+"F0.wireOp",EDGE,"E20.12.1"),sQuery(id+"F0.wireOp",EDGE,"E20.12.2"),sQuery(id+"F0.wireOp",EDGE,"E20.12.3"),sQuery(id+"F0.wireOp",EDGE,"E20.12.4"),sQuery(id+"F0.wireOp",EDGE,"E20.12.5"),sQuery(id+"F0.wireOp",EDGE,"E20.12.6"),sQuery(id+"F0.wireOp",EDGE,"E20.13.0"),sQuery(id+"F0.wireOp",EDGE,"E20.13.1"),sQuery(id+"F0.wireOp",EDGE,"E20.13.2"),sQuery(id+"F0.wireOp",EDGE,"E20.13.3"),sQuery(id+"F0.wireOp",EDGE,"E20.13.4"),sQuery(id+"F0.wireOp",EDGE,"E20.13.5"),sQuery(id+"F0.wireOp",EDGE,"E20.13.6")])],"isStart":false});
            var sketch = newSketch(context, id + "F2", { "sketchPlane" : qUnion([Q0])});
            skCircle(sketch, "E21", {"center": v(0, 0) * mm, "radius": 1.1 * mm});
            skSolve(sketch);
        }
        {
            var Q0;
            Q0=qSketchRegion(id+"F2",true);
            extrude(context, id + "F3", {"entities" : qUnion([Q0]), "operationType" : NewBodyOperationType.REMOVE, "endBound" : BoundingType.THROUGH_ALL, "oppositeDirection" : true, "depth" : 25 * mm});
        }
    });
